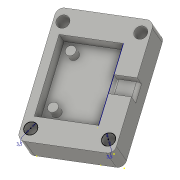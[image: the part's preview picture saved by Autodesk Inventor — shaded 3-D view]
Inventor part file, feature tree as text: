
AUTODESK INVENTOR PART (.ipt)
format: ipt  version: 2016 (Build 200138000, 138)  size: 159,232 bytes
history: native  units: mm
features: sketch x12, extrude x9, fillet x6
ambient origin geometry x8: Origin, YZ Plane, XZ Plane, XY Plane, X Axis, Y Axis, Z Axis, Center Point
bodies: Solid1 (feature_tree)
feature tree (27):
  sketch  "Sketch1"  dims[d0=35.0mm d1=25.0mm]
  extrude  "Extrusion1"  Depth=25.0mm
  extrude  "Extrusion2"  Depth=21.5mm
  sketch  "Sketch4"  dims[d33=2.0mm d34=0.5mm]
  sketch  "Sketch5"  dims[d47=3.5mm d48=3.5mm]
  extrude  "Extrusion9"  Depth=4.0mm TaperAngle=0.0deg
  fillet  "Fillet1"  Radius=5.0mm
  fillet  "Fillet2"  Radius=2.5mm
  fillet  "Fillet3"  Radius=2.0mm
  fillet  "Fillet4"  Radius=2.0mm
  fillet  "Fillet5"  Radius=2.0mm
  sketch  "Sketch13"  dims[d53=3.5mm d54=20.0mm d55=0.0mm]
  sketch  "Skizze18"  dims[d56=3.5mm d57=20.0mm d58=0.0mm]
  extrude  "Extrusion14"  Depth=0.5mm
  extrude  "Extrusion15"  Depth=3.5mm
  extrude  "Extrusion16"  Depth=20.0mm TaperAngle=0.0deg
  extrude  "Extrusion17"  Depth=20.0mm TaperAngle=0.0deg
  extrude  "Extrusion18"  Depth=20.0mm TaperAngle=0.0deg
  extrude  "Extrusion19"  Depth=3.0mm TaperAngle=0.0deg
  fillet  "Rundung6"  Radius=2.7mm
  sketch  "Sketch2"  dims[d2=8.0mm d3=0.0mm d4=21.5mm]
  sketch  "Sketch3"  dims[d5=16.5mm d6=4.0mm d7=0.0mm d27=5.0mm d28=2.5mm d29=0.0mm d30=2.0mm d31=2.0mm d32=2.0mm]
  sketch  "Sketch12"  dims[d49=20.0mm d50=0.0mm d51=20.0mm d52=0.0mm]
  sketch  "Skizze19"  dims[d59=2.7mm d60=3.0mm d61=0.0mm d62=2.7mm]
  sketch  "Skizze20"  dims[d63=2.7mm d64=0.0mm]
  sketch  "Skizze21"  dims[d65=1.0mm]
  sketch  "Skizze22"
